# Revit family: FA_МолниеотводСекционныйЛегкаяСерия_СМСПс_EZETEK
name_source: partatom
category: Системы пожарной сигнализации
revit_build: Autodesk Revit 2017 (Build: 20170118_1100(x64)
units: mm (PartAtom-declared; Revit-internal decimal feet)

## family parameters
Всегда вертикально = Да
На основе рабочей плоскости = Нет
Общий = Нет
При загрузке вырезать с полостями = Нет
Размер круглого соединителя = Использовать радиус
Сохранять ориентацию аннотаций = Нет
Тип детали = Нормальный
Точка расчета площади = Нет

## types (8) — shared parameters
ADSK_Версия Revit = 2017
ADSK_Единица измерения = шт.
ADSK_Завод-изготовитель = Ezetek
ADSK_Количество = 1
ADSK_Материал = BIMLIB_Алюминий_EZETEK
URL = https://ezetek.ru
Высота_Молниеприемник = 500 мм
Группа модели = Мачты на кронштейнах
Диаметр_1 секция = 90 мм
Диаметр_2 секция = 75 мм
Изготовитель = Ezetek
Секция 2 = Да
Угол = 90.00°

## per-type parameters (varying)
| type | ADSK_Код изделия | ADSK_Марка | ADSK_Масса | ADSK_Масса_Текст | ADSK_Наименование | ADSK_Обозначение | ADSK_Размер_Высота | Высота_3 секция | Высота_Кронштейны | Высота_Секция | Диаметр_3 секция | Количество секций | Описание | Секция 3 |
| МолниеотводСекционный_СМСПс-6.5/2_82122 | 82122 | 82122 | 20.5 | 20.5 | Молниеотвод стеновой СМСПс-6.5/2 | 82122 | 6000 мм | 500 мм | 650 мм | 3000 мм | 16 мм | 2 | Молниеотвод с мачтой серии СМС высотой 6 метров. Диаметр нижней секции - 75 мм, верхней - 60 мм. На верхней секции расположен молниеприемник 0,5 м диаметром 16 мм. 

Мачта молниеотвода  выполнена из труб алюминиевого сплава и дополнительно имеет защитное полимерное покрытие.

Молниеотвод устанавливается на кронштейны, которые входят в комплект поставки. В конструкции предусмотрен зажим для подключения заземлителя - полосы шириной до 40 мм или прутка. | Нет |
| МолниеотводСекционный_СМСПс-7.5/2_82132 | 82132 | 82132 | 25.3 | 25.3 | Молниеотвод стеновой СМСПс-7.5/2 | 82132 | 7000 мм | 500 мм | 750 мм | 3500 мм | 16 мм | 2 | Молниеотвод с мачтой серии СМС высотой 7 метров.  Диаметр нижней секции - 75 мм, верхней - 60 мм. На верхней секции расположен молниеприемник 0,5 м диаметром 16 мм. 

Мачта молниеотвода  выполнена из труб алюминиевого сплава и дополнительно имеет защитное полимерное покрытие.

Молниеотвод устанавливается на кронштейны, которые входят в комплект поставки. В конструкции предусмотрен зажим для подключения заземлителя - полосы шириной до 40 мм или прутка. | Нет |
| МолниеотводСекционный_СМСПс-8.5/3_82142 | 82142 | 82142 | 29.7 | 29.7 | Молниеотвод стеновой СМСПс-7.5/2 | 82142 | 8000 мм | 2667 мм | 850 мм | 2667 мм | 60 мм | 3 | Молниеотвод с мачтой серии СМС высотой 8 метров. Диаметр нижней секции - 90 мм, средней - 75 мм, верхней - 60 мм. На верхней секции расположен молниеприемник 0.5 м диаметром 16 мм. 

Мачта молниеотвода  выполнена из труб алюминиевого сплава и дополнительно имеет защитное полимерное покрытие.

Молниеотвод устанавливается на кронштейны, которые входят в комплект поставки. В конструкции предусмотрен зажим для подключения заземлителя - полосы шириной до 40 мм или прутка. | Да |
| МолниеотводСекционный_СМСПс-10,5/3_82162 | 82162 | 82162 | 38 | 38.0 | Молниеотвод стеновой СМСПс-10,5/3 | 82162 | 10000 мм | 3333 мм | 1050 мм | 3333 мм | 60 мм | 3 | Молниеотвод с мачтой серии СМС высотой 10 метров  Диаметр нижней секции - 90 мм, средней - 75 мм, верхней - 60 мм. На верхней секции расположен молниеприемник 0.5 м диаметром 16 мм. 

Мачта молниеотвода  выполнена из труб алюминиевого сплава и дополнительно имеет защитное полимерное покрытие.

Молниеотвод устанавливается на кронштейны, которые входят в комплект поставки. В конструкции предусмотрен зажим для подключения заземлителя - полосы шириной до 40 мм или прутка. | Да |
| МолниеотводСекционный_СМСПс-11,5/3_82172 | 82172 | 82172 | 45 | 45.0 | Молниеотвод стеновой СМСПс-11,5/3 | 82172 | 11000 мм | 3667 мм | 1150 мм | 3667 мм | 60 мм | 3 | Молниеотвод с мачтой серии СМС высотой 11 метров.  Диаметр нижней секции - 90 мм, средней - 75 мм, верхней - 60 мм. На верхней секции расположен молниеприемник 0.5 м диаметром 16 мм. 

Мачта молниеотвода  выполнена из труб алюминиевого сплава и дополнительно имеет защитное полимерное покрытие.

Молниеотвод устанавливается на кронштейны, которые входят в комплект поставки. В конструкции предусмотрен зажим для подключения заземлителя - полосы шириной до 40 мм или прутка. | Да |
| МолниеотводСекционный_СМСПс-12,5/3_82182 | 82182 | 82182 | 49 | 49.0 | Молниеотвод стеновой СМСПс-12,5/3 | 82182 | 12000 мм | 4000 мм | 1250 мм | 4000 мм | 60 мм | 3 | Молниеотвод с мачтой серии СМС высотой 12 метров.  Диаметр нижней секции - 90 мм, средней - 75 мм, верхней - 60 мм. На верхней секции расположен молниеприемник 0.5 м диаметром 16 мм. 

Мачта молниеотвода  выполнена из труб алюминиевого сплава и дополнительно имеет защитное полимерное покрытие.

Молниеотвод устанавливается на кронштейны, которые входят в комплект поставки. В конструкции предусмотрен зажим для подключения заземлителя - полосы шириной до 40 мм или прутка. | Да |
| МолниеотводСекционный_СМСПс-13,5/3_82192 | 82192 | 82192 | 53 | 53.0 | Молниеотвод стеновой СМСПс-13,5/3 | 82192 | 13000 мм | 4333 мм | 1350 мм | 4333 мм | 60 мм | 3 | Молниеотвод с мачтой серии СМС высотой 13 метров. Диаметр нижней секции - 90 мм, средней - 75 мм, верхней - 60 мм. На верхней секции расположен молниеприемник 0.5 м диаметром 16 мм. 

Мачта молниеотвода  выполнена из труб алюминиевого сплава и дополнительно имеет защитное полимерное покрытие.

Молниеотвод устанавливается на кронштейны, которые входят в комплект поставки. В конструкции предусмотрен зажим для подключения заземлителя - полосы шириной до 40 мм или прутка. | Да |
| МолниеотводСекционный_СМСПс-9.5/3_82152 | 82152 | 82152 | 33 | 33.0 | Молниеотвод стеновой СМСПс-7.5/2 | 82152 | 9000 мм | 3000 мм | 950 мм | 3000 мм | 60 мм | 3 | Молниеотвод с мачтой серии СМС высотой 9 метров. Диаметр нижней секции - 90 мм, средней - 75 мм, верхней - 60 мм. На верхней секции расположен молниеприемник 0.5 м диаметром 16 мм. 

Мачта молниеотвода  выполнена из труб алюминиевого сплава и дополнительно имеет защитное полимерное покрытие.

Молниеотвод устанавливается на кронштейны, которые входят в комплект поставки. В конструкции предусмотрен зажим для подключения заземлителя - полосы шириной до 40 мм или прутка. | Да |
